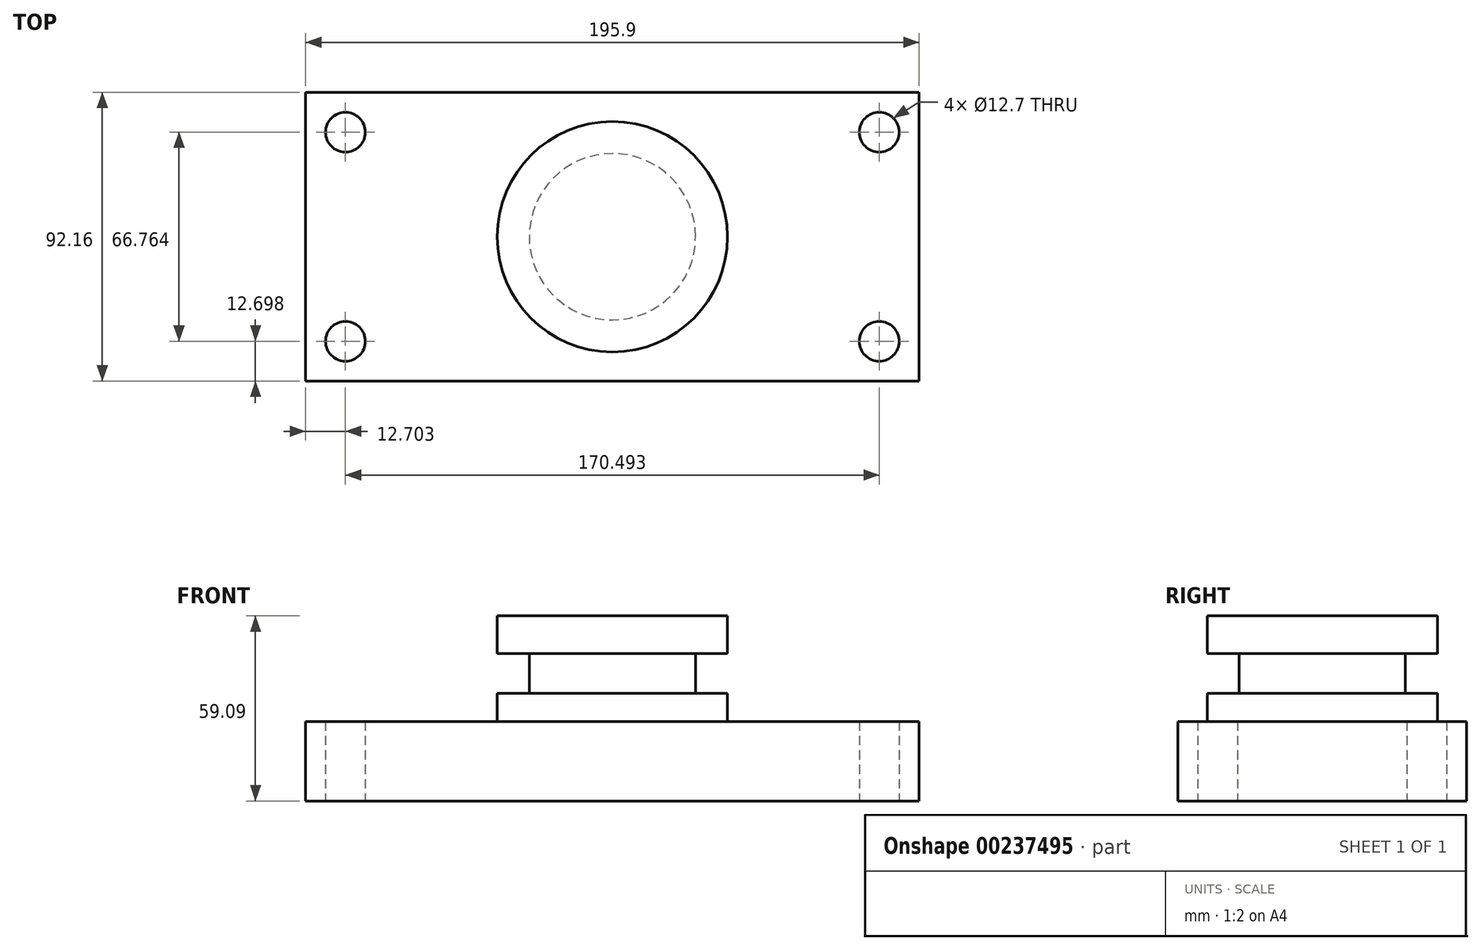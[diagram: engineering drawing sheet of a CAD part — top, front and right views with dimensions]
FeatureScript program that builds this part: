
annotation { "Feature Type Name" : "Feature", "Feature Type Description" : "" }
export const myFeature = defineFeature(function(context is Context, id is Id, definition is map)
    precondition{}
    {
        {
            var Q0;
            Q0=qCreatedBy(makeId("Top.planeOp"),FACE);
            var sketch = newSketch(context, id + "F0", { "sketchPlane" : qUnion([Q0])});
            skLineSegment(sketch, "E0.bottom", {"start": v(97.95, 46.08) * mm, "end": v(-97.95, 46.08) * mm});
            skLineSegment(sketch, "E0.top", {"start": v(97.95, -46.08) * mm, "end": v(-97.95, -46.08) * mm});
            skLineSegment(sketch, "E0.left", {"start": v(97.95, 46.08) * mm, "end": v(97.95, -46.08) * mm});
            skLineSegment(sketch, "E0.right", {"start": v(-97.95, 46.08) * mm, "end": v(-97.95, -46.08) * mm});
            skPoint(sketch, "E0.middle", {"position": v(0, 0) * mm});
            skSolve(sketch);
        }
        {
            var Q0;
            Q0=makeQuery(id+"F0.imprint","IMPRINT",FACE,{"disambiguationData":[TD([[makeQuery(id+"F0.imprint","IMPRINT",EDGE,{"derivedFrom":sQuery(id+"F0.wireOp",EDGE,"E0.bottom")}),1.0]])]});
            extrude(context, id + "F1", {"entities" : qUnion([Q0]), "depth" : 25.4 * mm});
        }
        {
            var Q0;
            Q0=qCreatedBy(makeId("Top.planeOp"),FACE);
            var sketch = newSketch(context, id + "F2", { "sketchPlane" : qUnion([Q0])});
            skCircle(sketch, "E1", {"center": v(-85.25, 33.38) * mm, "radius": 6.35 * mm});
            skCircle(sketch, "E2", {"center": v(-85.25, -33.38) * mm, "radius": 6.35 * mm});
            skCircle(sketch, "E3", {"center": v(85.25, 33.38) * mm, "radius": 6.35 * mm});
            skCircle(sketch, "E4", {"center": v(85.25, -33.38) * mm, "radius": 6.35 * mm});
            skSolve(sketch);
        }
        {
            var Q0;
            Q0 = qSketchRegion(id + "F2", true);
            extrude(context, id + "F3", {"entities" : qUnion([Q0]), "operationType" : NewBodyOperationType.REMOVE, "depth" : 25.4 * mm});
        }
        {
            var Q0;
            Q0=qCreatedBy(makeId("Front.planeOp"),FACE);
            var sketch = newSketch(context, id + "F4", { "sketchPlane" : qUnion([Q0])});
            skLineSegment(sketch, "E5.bottom", {"start": v(0, 59.09) * mm, "end": v(-36.79, 59.09) * mm});
            skLineSegment(sketch, "E5.top", {"start": v(0, 25.4) * mm, "end": v(-36.79, 25.4) * mm});
            skLineSegment(sketch, "E5.left", {"start": v(0, 59.09) * mm, "end": v(0, 25.4) * mm});
            skLineSegment(sketch, "E5.right", {"start": v(-36.79, 59.09) * mm, "end": v(-36.79, 25.4) * mm});
            skSolve(sketch);
        }
        {
            var Q0;
            Q0 = qSketchRegion(id + "F4", true);
            var Q1;
            Q1=sQuery(id+"F4.wireOp",EDGE,"E5.left");
            revolve(context, id + "F5", {"operationType" : NewBodyOperationType.ADD, "entities" : qUnion([Q0]), "axis" : qUnion([Q1]), "revolveType" : RevolveType.FULL});
        }
        {
            var Q0;
            Q0=qCreatedBy(makeId("Front.planeOp"),FACE);
            var sketch = newSketch(context, id + "F6", { "sketchPlane" : qUnion([Q0])});
            skLineSegment(sketch, "E6.bottom", {"start": v(-26.57, 47.08) * mm, "end": v(-51.99, 47.08) * mm});
            skLineSegment(sketch, "E6.top", {"start": v(-26.57, 34.37) * mm, "end": v(-51.99, 34.37) * mm});
            skLineSegment(sketch, "E6.left", {"start": v(-26.57, 47.08) * mm, "end": v(-26.57, 34.37) * mm});
            skLineSegment(sketch, "E6.right", {"start": v(-51.99, 47.08) * mm, "end": v(-51.99, 34.37) * mm});
            skSolve(sketch);
        }
        {
            var Q0;
            Q0=makeQuery(id+"F6.imprint","IMPRINT",FACE,{"disambiguationData":[TD([[makeQuery(id+"F6.imprint","IMPRINT",EDGE,{"derivedFrom":sQuery(id+"F6.wireOp",EDGE,"E6.bottom")}),1.0]])]});
            var Q1;
            Q1=makeQuery(id+"F5.opRevolve","SWEPT_FACE",FACE,{"disambiguationData":[OSD([sQuery(id+"F4.wireOp",EDGE,"E5.right")])]});
            revolve(context, id + "F7", {"operationType" : NewBodyOperationType.REMOVE, "entities" : qUnion([Q0]), "axis" : qUnion([Q1]), "revolveType" : RevolveType.FULL, "oppositeDirection" : true});
        }
    });
